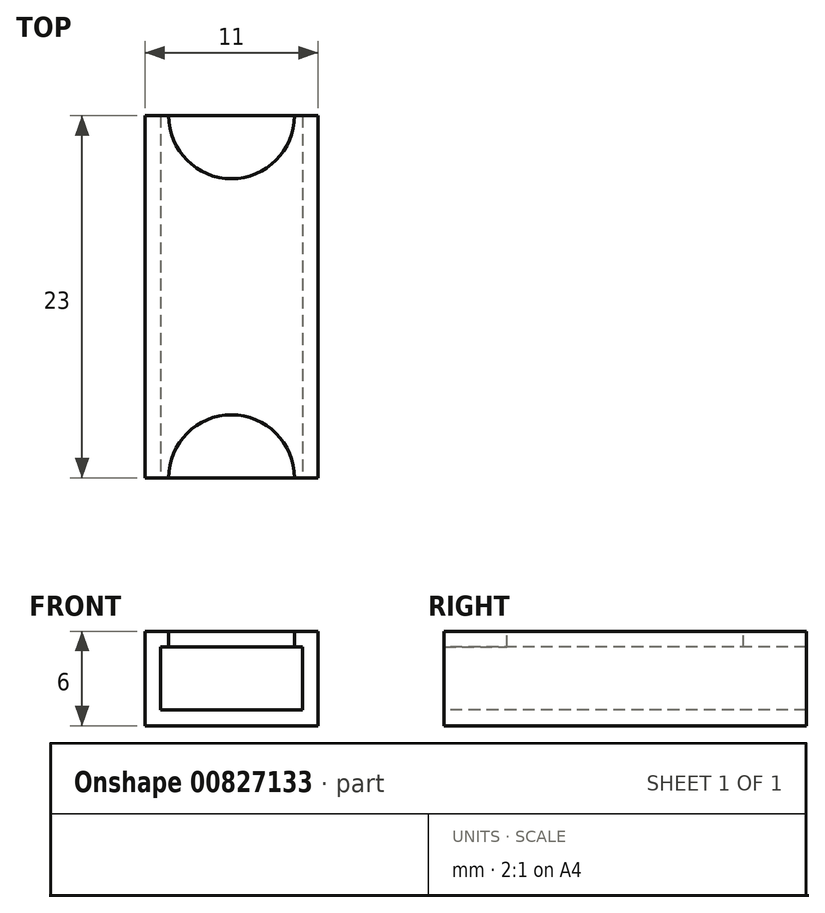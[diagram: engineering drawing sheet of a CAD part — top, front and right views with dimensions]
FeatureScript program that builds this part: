
annotation { "Feature Type Name" : "Feature", "Feature Type Description" : "" }
export const myFeature = defineFeature(function(context is Context, id is Id, definition is map)
    precondition{}
    {
        {
            var Q0;
            Q0=qCreatedBy(makeId("Top.planeOp"),FACE);
            var sketch = newSketch(context, id + "F0", { "sketchPlane" : qUnion([Q0])});
            skLineSegment(sketch, "E0.bottom", {"start": v(5.5, -11.5) * mm, "end": v(-5.5, -11.5) * mm});
            skLineSegment(sketch, "E0.top", {"start": v(5.5, 11.5) * mm, "end": v(-5.5, 11.5) * mm});
            skLineSegment(sketch, "E0.left", {"start": v(5.5, -11.5) * mm, "end": v(5.5, 11.5) * mm});
            skLineSegment(sketch, "E0.right", {"start": v(-5.5, -11.5) * mm, "end": v(-5.5, 11.5) * mm});
            skPoint(sketch, "E0.middle", {"position": v(0, 0) * mm});
            skSolve(sketch);
        }
        {
            var Q0;
            Q0 = qSketchRegion(id + "F0", true);
            extrude(context, id + "F1", {"entities" : qUnion([Q0]), "depth" : 6 * mm, "offsetDistance" : 25 * mm});
        }
        {
            var Q0;
            Q0=makeQuery(id+"F1.opExtrude","SWEPT_FACE",FACE,{"disambiguationData":[OSD([sQuery(id+"F0.wireOp",EDGE,"E0.bottom")])]});
            var sketch = newSketch(context, id + "F2", { "sketchPlane" : qUnion([Q0])});
            skLineSegment(sketch, "E1.bottom", {"start": v(4.5, 1) * mm, "end": v(-4.5, 1) * mm});
            skLineSegment(sketch, "E1.top", {"start": v(4.5, 5) * mm, "end": v(-4.5, 5) * mm});
            skLineSegment(sketch, "E1.left", {"start": v(4.5, 1) * mm, "end": v(4.5, 5) * mm});
            skLineSegment(sketch, "E1.right", {"start": v(-4.5, 1) * mm, "end": v(-4.5, 5) * mm});
            skPoint(sketch, "E1.middle", {"position": v(0, 3) * mm});
            skLineSegment(sketch, "E2", {"start": v(0, 0) * mm, "end": v(0, 3) * mm, "construction": true});
            skLineSegment(sketch, "E3", {"start": v(0, 3) * mm, "end": v(0, 6) * mm, "construction": true});
            skSolve(sketch);
        }
        {
            var Q0;
            Q0 = qSketchRegion(id + "F2", true);
            extrude(context, id + "F3", {"entities" : qUnion([Q0]), "operationType" : NewBodyOperationType.REMOVE, "endBound" : BoundingType.THROUGH_ALL, "oppositeDirection" : true, "depth" : 25 * mm, "offsetDistance" : 25 * mm});
        }
        {
            var Q0;
            Q0=makeQuery(id+"F1.opExtrude","CAP_FACE",FACE,{"disambiguationData":[OSD([sQuery(id+"F0.wireOp",EDGE,"E0.bottom"),sQuery(id+"F0.wireOp",EDGE,"E0.top"),sQuery(id+"F0.wireOp",EDGE,"E0.left"),sQuery(id+"F0.wireOp",EDGE,"E0.right")])],"isStart":false});
            var sketch = newSketch(context, id + "F4", { "sketchPlane" : qUnion([Q0])});
            skLineSegment(sketch, "E4", {"start": v(-4, 11.5) * mm, "end": v(4, 11.5) * mm});
            skArc(sketch, "E5", {"start": v(-4, 11.5) * mm, "mid": v(0, 7.5) * mm, "end": v(4, 11.5) * mm});
            skArc(sketch, "E6.MirrorCS", {"start": v(-4, -11.5) * mm, "mid": v(0, -7.5) * mm, "end": v(4, -11.5) * mm});
            skLineSegment(sketch, "E7.MirrorCS", {"start": v(-4, -11.5) * mm, "end": v(4, -11.5) * mm});
            skSolve(sketch);
        }
        {
            var Q0;
            Q0 = qSketchRegion(id + "F4", true);
            extrude(context, id + "F5", {"entities" : qUnion([Q0]), "operationType" : NewBodyOperationType.REMOVE, "oppositeDirection" : true, "depth" : 1.5 * mm, "offsetDistance" : 25 * mm});
        }
    });
